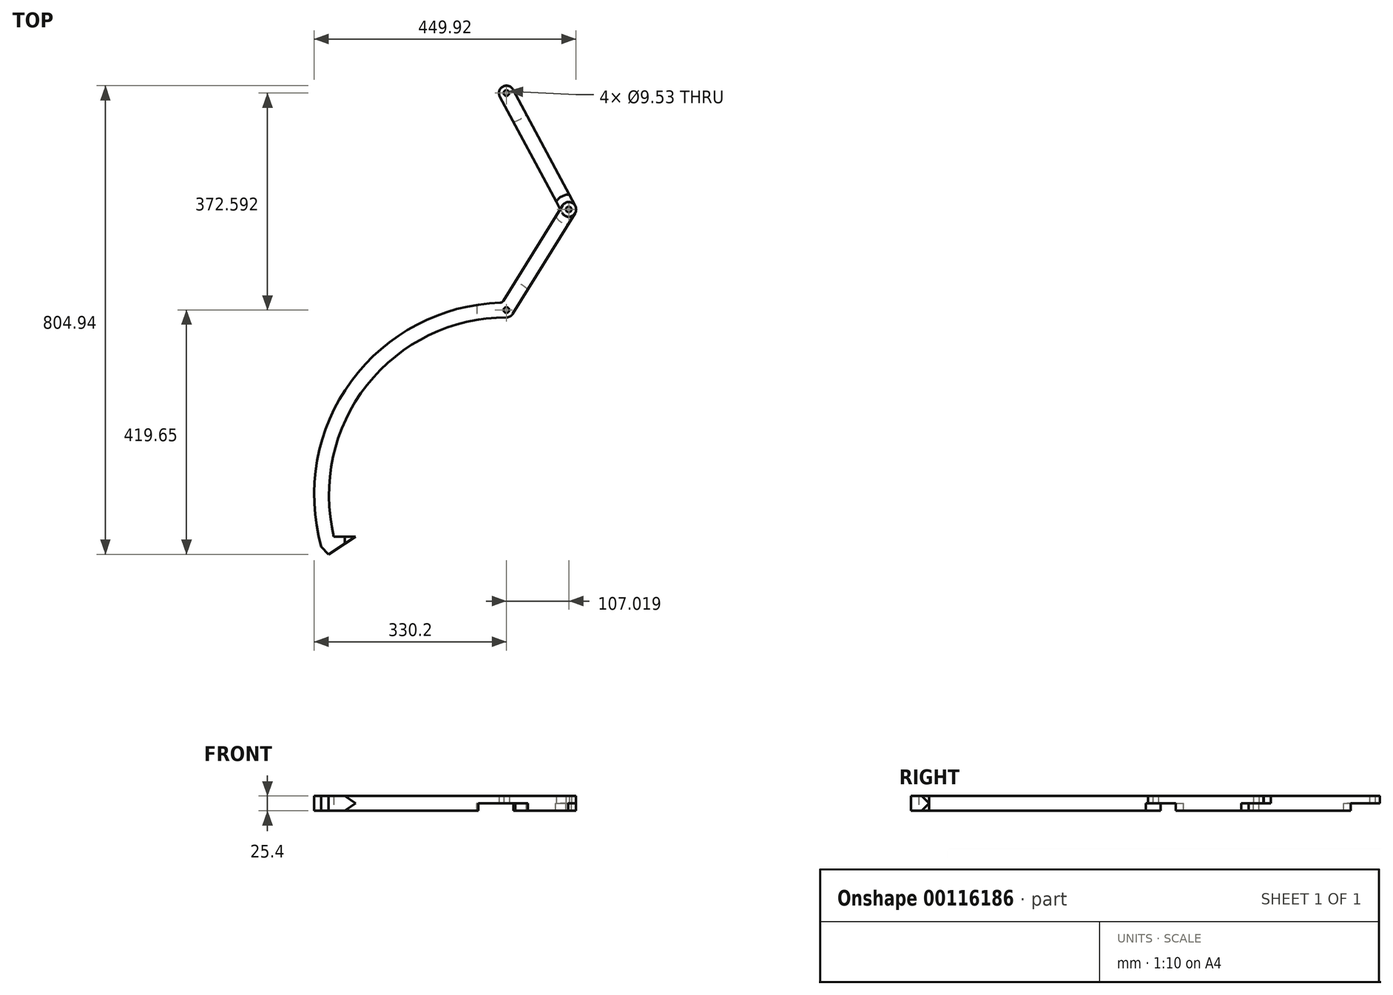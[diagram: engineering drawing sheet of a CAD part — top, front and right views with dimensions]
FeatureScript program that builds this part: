
annotation { "Feature Type Name" : "Feature", "Feature Type Description" : "" }
export const myFeature = defineFeature(function(context is Context, id is Id, definition is map)
    precondition{}
    {
        {
            var Q0;
            Q0=qCreatedBy(makeId("Top.planeOp"),FACE);
            var sketch = newSketch(context, id + "F0", { "sketchPlane" : qUnion([Q0])});
            skArc(sketch, "E0", {"start": v(-296.3, -71.48) * mm, "mid": v(-239.47, 188.57) * mm, "end": v(0, 304.8) * mm});
            skArc(sketch, "E1.0", {"start": v(-317.96, -89.07) * mm, "mid": v(-266.24, 195.31) * mm, "end": v(-10.51, 330.03) * mm});
            skLineSegment(sketch, "E2", {"start": v(-296.3, -71.48) * mm, "end": v(-259.2, -71.48) * mm});
            skLineSegment(sketch, "E3", {"start": v(-259.2, -71.48) * mm, "end": v(-305.74, -102.15) * mm});
            skLineSegment(sketch, "E4", {"start": v(-305.74, -102.15) * mm, "end": v(-317.96, -89.07) * mm});
            skCircle(sketch, "E5", {"center": v(0, 317.5) * mm, "radius": 4.76 * mm});
            skPoint(sketch, "E5.centerSnap0", {"position": v(0, 330.2) * mm});
            skArc(sketch, "E6", {"start": v(0, 304.8) * mm, "mid": v(6.18, 306.4) * mm, "end": v(10.8, 310.81) * mm});
            skLineSegment(sketch, "E7", {"start": v(0, 0) * mm, "end": v(0, 690.1) * mm, "construction": true});
            skArc(sketch, "E8", {"start": v(117.82, 483.55) * mm, "mid": v(113.7, 501.03) * mm, "end": v(96.22, 496.92) * mm});
            skLineSegment(sketch, "E9", {"start": v(10.8, 310.81) * mm, "end": v(117.82, 483.55) * mm});
            skLineSegment(sketch, "E10", {"start": v(-5.32, 333.04) * mm, "end": v(96.22, 496.92) * mm});
            skLineSegment(sketch, "E11", {"start": v(24.65, 317.5) * mm, "end": v(-26.35, 317.5) * mm, "construction": true});
            skPoint(sketch, "E12.visualSharp", {"position": v(-7.12, 330.12) * mm});
            skArc(sketch, "E12.filletArc", {"start": v(-10.51, 330.03) * mm, "mid": v(-7.54, 330.88) * mm, "end": v(-5.32, 333.04) * mm});
            skCircle(sketch, "E13", {"center": v(107.02, 490.23) * mm, "radius": 4.76 * mm});
            skCircle(sketch, "E14", {"center": v(0, 690.1) * mm, "radius": 12.7 * mm});
            skCircle(sketch, "E15", {"center": v(0, 690.1) * mm, "radius": 4.76 * mm});
            skCircle(sketch, "E16", {"center": v(107.02, 490.23) * mm, "radius": 12.7 * mm});
            skLineSegment(sketch, "E17", {"start": v(-11.2, 684.1) * mm, "end": v(95.82, 484.24) * mm});
            skLineSegment(sketch, "E18", {"start": v(118.22, 496.23) * mm, "end": v(11.2, 696.09) * mm});
            skArc(sketch, "E19", {"start": v(-50.02, 326.39) * mm, "mid": v(-50.65, 313.56) * mm, "end": v(-48.04, 301) * mm});
            skArc(sketch, "E20.trimOffspring", {"start": v(36.7, 352.62) * mm, "mid": v(26.75, 360.68) * mm, "end": v(15.1, 366) * mm});
            skArc(sketch, "E21", {"start": v(84.64, 478.22) * mm, "mid": v(93.64, 468.64) * mm, "end": v(106.23, 464.85) * mm});
            skArc(sketch, "E22.trimOffspring", {"start": v(107.83, 515.62) * mm, "mid": v(95.03, 512.63) * mm, "end": v(85.44, 503.63) * mm});
            skArc(sketch, "E23", {"start": v(12.02, 640.74) * mm, "mid": v(23.98, 645.3) * mm, "end": v(34.42, 652.73) * mm});
            skSolve(sketch);
        }
        {
            var Q0;
            {var subQ0=sQuery(id+"F0.wireOp",EDGE,"E20.trimOffspring");Q0=makeQuery(id+"F0.imprint","IMPRINT",FACE,{"disambiguationData":[TD([[makeQuery(id+"F0.imprint","IMPRINT",EDGE,{"derivedFrom":subQ0}),-1.0]])]});}
            var Q1;
            {var subQ7=sQuery(id+"F0.wireOp",EDGE,"E21");Q1=makeQuery(id+"F0.imprint","IMPRINT",FACE,{"disambiguationData":[TD([[makeQuery(id+"F0.imprint","IMPRINT",EDGE,{"derivedFrom":subQ7}),1.0]])]});}
            var Q2;
            Q2=makeQuery(id+"F0.imprint","IMPRINT",FACE,{"disambiguationData":[TD([[makeQuery(id+"F0.imprint","IMPRINT",EDGE,{"derivedFrom":sQuery(id+"F0.wireOp",EDGE,"E13")}),-1.0]])]});
            var Q3;
            {var subQ0=sQuery(id+"F0.wireOp",EDGE,"E16");var subQ1=sQuery(id+"F0.wireOp",EDGE,"E10");var subQ2=makeQuery(id+"F0.imprint","INTERSECT",VERTEX,{"derivedFrom":[subQ1,subQ0]});Q3=makeQuery(id+"F0.imprint","IMPRINT",FACE,{"disambiguationData":[TD([[makeQuery(id+"F0.imprint","IMPRINT",EDGE,{"disambiguationData":[TD([[subQ2,1.0]])],"derivedFrom":subQ1}),-1.0]])]});}
            var Q4;
            Q4=makeQuery(id+"F0.imprint","IMPRINT",FACE,{"disambiguationData":[TD([[makeQuery(id+"F0.imprint","IMPRINT",EDGE,{"derivedFrom":sQuery(id+"F0.wireOp",EDGE,"E5")}),-1.0]])]});
            var Q5;
            {var subQ0=sQuery(id+"F0.wireOp",EDGE,"E2");Q5=makeQuery(id+"F0.imprint","IMPRINT",FACE,{"disambiguationData":[TD([[makeQuery(id+"F0.imprint","IMPRINT",EDGE,{"derivedFrom":subQ0}),-1.0]])]});}
            extrude(context, id + "F1", {"entities" : qUnion([Q0, Q1, Q2, Q3, Q4, Q5]), "depth" : 12.7 * mm});
        }
        {
            var Q0;
            {var subQ0=sQuery(id+"F0.wireOp",EDGE,"E20.trimOffspring");Q0=makeQuery(id+"F0.imprint","IMPRINT",FACE,{"disambiguationData":[TD([[makeQuery(id+"F0.imprint","IMPRINT",EDGE,{"derivedFrom":subQ0}),-1.0]])]});}
            var Q1;
            {var subQ0=sQuery(id+"F0.wireOp",EDGE,"E2");Q1=makeQuery(id+"F0.imprint","IMPRINT",FACE,{"disambiguationData":[TD([[makeQuery(id+"F0.imprint","IMPRINT",EDGE,{"derivedFrom":subQ0}),-1.0]])]});}
            extrude(context, id + "F2", {"entities" : qUnion([Q0, Q1]), "operationType" : NewBodyOperationType.ADD, "oppositeDirection" : true, "depth" : 12.7 * mm});
        }
        {
            var Q0;
            {var subQ0=sQuery(id+"F0.wireOp",EDGE,"E22.trimOffspring");Q0=makeQuery(id+"F0.imprint","IMPRINT",FACE,{"disambiguationData":[TD([[makeQuery(id+"F0.imprint","IMPRINT",EDGE,{"derivedFrom":subQ0}),-1.0]])]});}
            var Q1;
            {var subQ5=sQuery(id+"F0.wireOp",EDGE,"E22.trimOffspring");Q1=makeQuery(id+"F0.imprint","IMPRINT",FACE,{"disambiguationData":[TD([[makeQuery(id+"F0.imprint","IMPRINT",EDGE,{"derivedFrom":subQ5}),1.0]])]});}
            var Q2;
            {var subQ0=sQuery(id+"F0.wireOp",EDGE,"E16");var subQ1=sQuery(id+"F0.wireOp",EDGE,"E10");var subQ2=makeQuery(id+"F0.imprint","INTERSECT",VERTEX,{"derivedFrom":[subQ1,subQ0]});Q2=makeQuery(id+"F0.imprint","IMPRINT",FACE,{"disambiguationData":[TD([[makeQuery(id+"F0.imprint","IMPRINT",EDGE,{"disambiguationData":[TD([[subQ2,1.0]])],"derivedFrom":subQ1}),-1.0]])]});}
            var Q3;
            Q3=makeQuery(id+"F0.imprint","IMPRINT",FACE,{"disambiguationData":[TD([[makeQuery(id+"F0.imprint","IMPRINT",EDGE,{"derivedFrom":sQuery(id+"F0.wireOp",EDGE,"E13")}),-1.0]])]});
            extrude(context, id + "F3", {"entities" : qUnion([Q0, Q1, Q2, Q3]), "oppositeDirection" : true, "depth" : 12.7 * mm});
        }
        {
            var Q0;
            {var subQ0=sQuery(id+"F0.wireOp",EDGE,"E22.trimOffspring");Q0=makeQuery(id+"F0.imprint","IMPRINT",FACE,{"disambiguationData":[TD([[makeQuery(id+"F0.imprint","IMPRINT",EDGE,{"derivedFrom":subQ0}),-1.0]])]});}
            var Q1;
            {var subQ5=sQuery(id+"F0.wireOp",EDGE,"E23");Q1=makeQuery(id+"F0.imprint","IMPRINT",FACE,{"disambiguationData":[TD([[makeQuery(id+"F0.imprint","IMPRINT",EDGE,{"derivedFrom":subQ5}),1.0]])]});}
            var Q2;
            Q2=makeQuery(id+"F0.imprint","IMPRINT",FACE,{"disambiguationData":[TD([[makeQuery(id+"F0.imprint","IMPRINT",EDGE,{"derivedFrom":sQuery(id+"F0.wireOp",EDGE,"E15")}),-1.0]])]});
            extrude(context, id + "F4", {"entities" : qUnion([Q0, Q1, Q2]), "operationType" : NewBodyOperationType.ADD, "depth" : 12.7 * mm});
        }
        {
            var Q0;
            {var subQ0=sQuery(id+"F0.wireOp",EDGE,"E2");Q0=makeQuery(id+"F2.boolean.opBoolean","MERGE",FACE,{"derivedFrom":[makeQuery(id+"F1.opExtrude","SWEPT_FACE",FACE,{"disambiguationData":[OSD([subQ0])]}),makeQuery(id+"F2.opExtrude","SWEPT_FACE",FACE,{"disambiguationData":[OSD([subQ0])]})]});}
            var sketch = newSketch(context, id + "F5", { "sketchPlane" : qUnion([Q0])});
            skLineSegment(sketch, "E24", {"start": v(259.2, 0) * mm, "end": v(277.75, 12.7) * mm});
            skLineSegment(sketch, "E25", {"start": v(259.2, 0) * mm, "end": v(277.75, -12.7) * mm});
            skSolve(sketch);
        }
        {
            var Q0;
            {var subQ0=sQuery(id+"F5.wireOp",EDGE,"E24");Q0=makeQuery(id+"F5.imprint","IMPRINT",FACE,{"disambiguationData":[TD([[makeQuery(id+"F5.imprint","IMPRINT",EDGE,{"derivedFrom":subQ0}),1.0]])]});}
            var Q1;
            {var subQ0=sQuery(id+"F5.wireOp",EDGE,"E25");Q1=makeQuery(id+"F5.imprint","IMPRINT",FACE,{"disambiguationData":[TD([[makeQuery(id+"F5.imprint","IMPRINT",EDGE,{"derivedFrom":subQ0}),-1.0]])]});}
            extrude(context, id + "F6", {"entities" : qUnion([Q0, Q1]), "operationType" : NewBodyOperationType.REMOVE, "endBound" : BoundingType.THROUGH_ALL, "oppositeDirection" : true, "depth" : 25.4 * mm});
        }
    });
